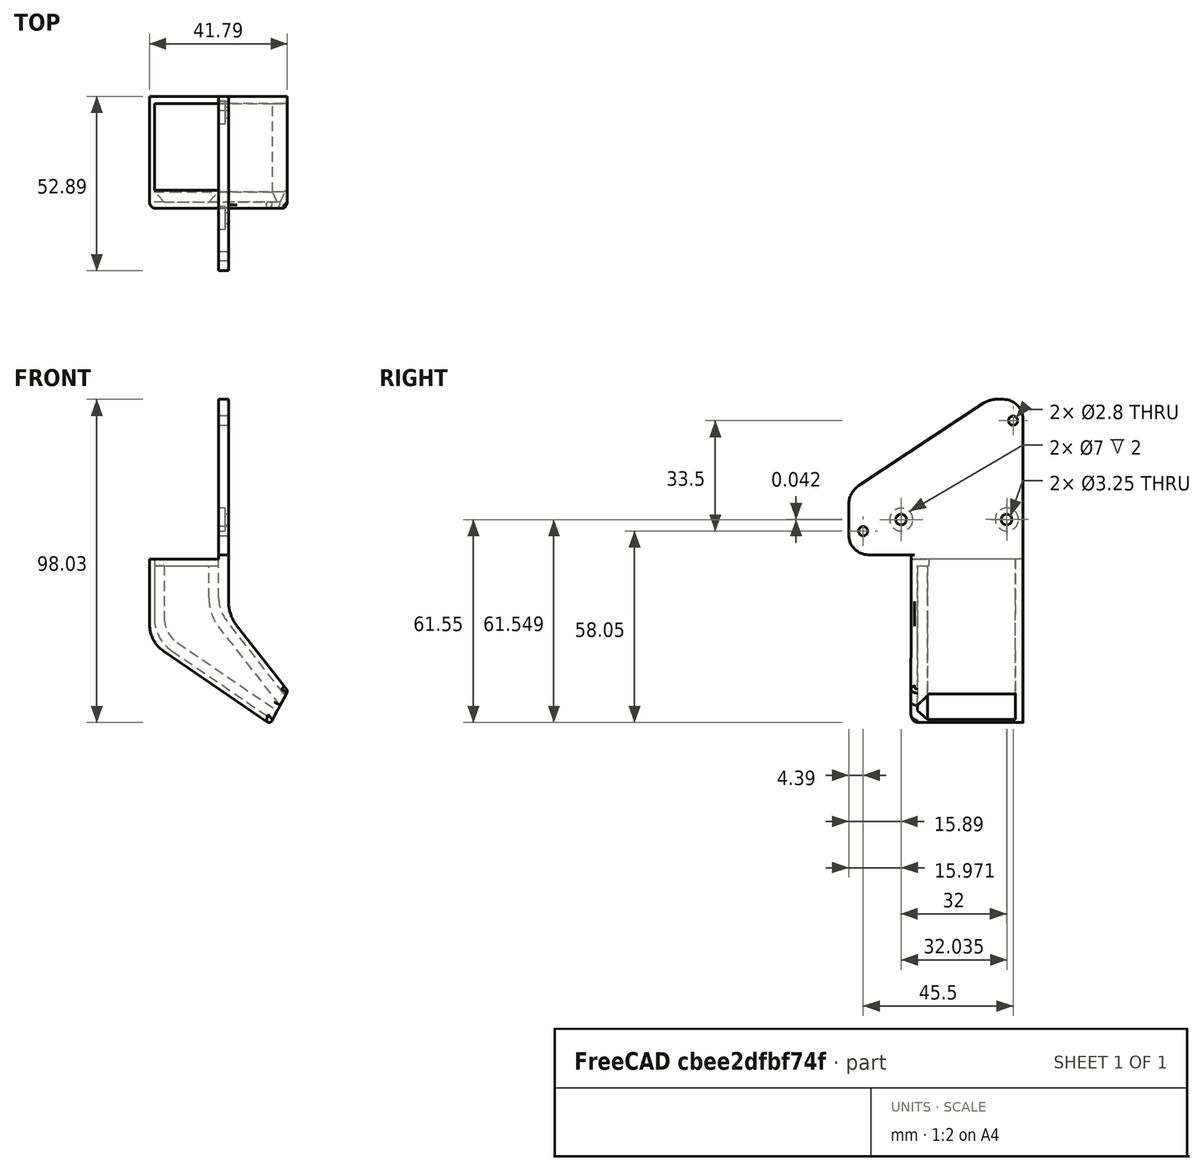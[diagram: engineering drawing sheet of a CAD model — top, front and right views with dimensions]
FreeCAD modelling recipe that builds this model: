
FCSTD DOCUMENT  (FreeCAD 0.19R)
Label: FanDuct10.1
License: All rights reserved
LicenseURL: http://en.wikipedia.org/wiki/All_rights_reserved
objects: Sketcher::SketchObject×10, PartDesign::Fillet×10, PartDesign::Pocket×5, PartDesign::Pad×3, PartDesign::Chamfer×2, PartDesign::Body×1, Mesh::Feature×1
note: 51 computed .brp shape members not serialized (recipe doc carries the construction recipe); baked Part::Feature solids carry a one-line shape summary decoded from their .brp

FEATURE [Sketcher::SketchObject] Sketch035  label="startingpos"
  FullyConstrained = false
  MapMode = 5
  Placement = pos=(-14,0,0) rot=(0.57735,-0.57735,-0.57735;2.0944rad)
  sketch-geometry (5):
    g0: Circle CenterX=35 CenterY=-20 CenterZ=0 NormalX=0 NormalY=0 NormalZ=1 AngleXU=0 Radius=1
    g1: Circle CenterX=12 CenterY=44 CenterZ=0 NormalX=0 NormalY=0 NormalZ=1 AngleXU=0 Radius=1.9
    g2: Circle CenterX=55 CenterY=44 CenterZ=0 NormalX=0 NormalY=0 NormalZ=1 AngleXU=0 Radius=1.9
    g3: LineSegment StartX=12.5 StartY=38 StartZ=0 EndX=35 EndY=38 EndZ=0
    g4: GeomPoint X=35 Y=-19 Z=0
  constraints (13):
    c: DistanceY(g0) = -20
    c: Diameter(g1) = 3.8
    c: Equal(g1,g2)
    c: DistanceY(g1) = 44
    c: DistanceX(g2) = 55
    c: DistanceY(g2) = 44
    c: Diameter(g0) = 2
    c: Horizontal(g3)
    c: Distance(g3) = 22.5
    c: DistanceX(g0) = 35
    c: DistanceX(g3) = 35
    c: DistanceY(g3) = 38
    c: DistanceX(g4) = 35
FEATURE [Sketcher::SketchObject] Sketch037  label="startingpos001"
  FullyConstrained = false
  MapMode = 5
  Placement = pos=(-35,0,2e-15) rot=(0.57735,-0.57735,-0.57735;2.0944rad)
  sketch-geometry (11):
    g0: Circle CenterX=35 CenterY=-20 CenterZ=0 NormalX=0 NormalY=0 NormalZ=1 AngleXU=0 Radius=1
    g1: Circle CenterX=12 CenterY=44 CenterZ=0 NormalX=0 NormalY=0 NormalZ=1 AngleXU=0 Radius=1.9
    g2: Circle CenterX=55 CenterY=44 CenterZ=0 NormalX=0 NormalY=0 NormalZ=1 AngleXU=0 Radius=1.9
    g3: LineSegment StartX=12.5 StartY=38 StartZ=0 EndX=35 EndY=38 EndZ=0
    g4: LineSegment StartX=5.72016 StartY=54.4932 StartZ=0 EndX=25.1498 EndY=-38.5121 EndZ=0
    g5: LineSegment StartX=25.1498 StartY=-38.5121 StartZ=0 EndX=-60.2156 EndY=-38.5121 EndZ=0
    g6: LineSegment StartX=-60.2156 StartY=-38.5121 StartZ=0 EndX=-35.1899 EndY=60.5708 EndZ=0
    g7: LineSegment StartX=-35.1899 StartY=60.5708 StartZ=0 EndX=99.6909 EndY=60.5708 EndZ=0
    g8: LineSegment StartX=56.1815 StartY=-38.9405 StartZ=0 EndX=37.0599 EndY=52.5904 EndZ=0
    g9: LineSegment StartX=56.1815 StartY=-38.9405 StartZ=0 EndX=99.6909 EndY=60.5708 EndZ=0
    g10: LineSegment StartX=5.72016 StartY=54.4932 StartZ=0 EndX=37.0599 EndY=52.5904 EndZ=0
  constraints (27):
    c: DistanceY(g0) = -20
    c: Diameter(g1) = 3.8
    c: Equal(g1,g2)
    c: DistanceX(g1) = 12
    c: DistanceY(g1) = 44
    c: DistanceX(g2) = 55
    c: DistanceY(g2) = 44
    c: Diameter(g0) = 2
    c: Horizontal(g3)
    c: Distance(g3) = 22.5
    c: DistanceX(g0) = 35
    c: DistanceX(g3) = 35
    c: DistanceY(g3) = 38
    c: Horizontal(g5)
    c: Coincident(g5,g6)
    c: Coincident(g6,g7)
    c: Horizontal(g7)
    c: Distance(g3,g8) = 5
    c: Coincident(g5,g4)
    c: Coincident(g8,g9)
    c: Coincident(g9,g7)
    c: DistanceX(g7) = 99.6909
    c: DistanceY(g7) = 60.5708
    c: DistanceX(g6) = -35.1899
    c: Parallel(g8,g4)
    c: Coincident(g10,g4)
    c: Coincident(g10,g8)
FEATURE [Sketcher::SketchObject] Sketch  label="Body001"
  FullyConstrained = false
  MapMode = 5
  Placement = pos=(0,0,0) rot=(1,0,0;1.5708rad)
  Support = -> [XZ_Plane]
  sketch-geometry (14):
    g0: LineSegment StartX=0 StartY=35 StartZ=0 EndX=-3 EndY=35 EndZ=0
    g1: LineSegment StartX=-3 StartY=35 StartZ=0 EndX=-3 EndY=-15 EndZ=0
    g2: LineSegment StartX=-3 StartY=-15 StartZ=0 EndX=-24 EndY=-15 EndZ=0
    g3: LineSegment StartX=-24 StartY=-15 StartZ=0 EndX=-24 EndY=-40 EndZ=0
    g4: GeomPoint X=25 Y=-66 Z=0
    g5: LineSegment StartX=0 StartY=0 StartZ=0 EndX=53.43 EndY=0 EndZ=0
    g6: LineSegment StartX=53.43 StartY=0 StartZ=0 EndX=53.43 EndY=-30 EndZ=0
    g7: LineSegment StartX=53.43 StartY=-30 StartZ=0 EndX=0 EndY=-30 EndZ=0
    g8: LineSegment StartX=0 StartY=-30 StartZ=0 EndX=0 EndY=0 EndZ=0
    g9: LineSegment StartX=0 StartY=0 StartZ=0 EndX=0 EndY=-32 EndZ=0
    g10: LineSegment StartX=0 StartY=-32 StartZ=0 EndX=18 EndY=-55 EndZ=0
    g11: LineSegment StartX=-24 StartY=-40 StartZ=0 EndX=12.6411 EndY=-65 EndZ=0
    g12: LineSegment StartX=12.6411 StartY=-65 StartZ=0 EndX=18 EndY=-55 EndZ=0
    g13: LineSegment StartX=0 StartY=35 StartZ=0 EndX=0 EndY=0 EndZ=0
  constraints (38):
    c: PointOnObject(g0,g-2)
    c: Coincident(g0,g1)
    c: Vertical(g1)
    c: Coincident(g1,g2)
    c: Horizontal(g2)
    c: Coincident(g2,g3)
    c: Vertical(g3)
    c: Horizontal(g0)
    c: Distance(g0) = 3
    c: DistanceX(g4) = 25
    c: DistanceY(g4) = -66
    c: Distance(g2) = 21
    c: Distance(g3) = 25
    c: DistanceY(g1) = -15
    c: Distance(g1) = 50
    c: Coincident(g5,g6)
    c: Coincident(g6,g7)
    c: Coincident(g7,g8)
    c: Coincident(g8,g5)
    c: Horizontal(g5)
    c: Horizontal(g7)
    c: Vertical(g6)
    c: Vertical(g8)
    c: DistanceY(g6) = -30
    c: Coincident(g5,g-1)
    c: Coincident(g-1,g9)
    c: Vertical(g9)
    c: Coincident(g9,g10)
    c: DistanceY(g4,g10) = 11
    c: DistanceX(g10,g4) = 7
    c: Coincident(g11,g3)
    c: DistanceY(g11,g4) = -1
    c: Coincident(g11,g12)
    c: Coincident(g12,g10)
    c: Distance(g9,g7) = 2
    c: DistanceX(g6) = 53.43
    c: Coincident(g0,g13)
    c: Coincident(g13,g9)
FEATURE [PartDesign::Pad] Pad
  Direction = (1,1,1)
  Length = 70
  Length2 = 100
  Placement = pos=(0,0,0) rot=(1,0,0;1.5708rad)
  Profile = -> Sketch
  Type = 0
FEATURE [Sketcher::SketchObject] Sketch052  label="Mountholes"
  FullyConstrained = true
  MapMode = 5
  Placement = pos=(-3,0,0) rot=(0.707107,0,-0.707107;3.14159rad)
  Support = -> [Pad]
  sketch-geometry (2):
    g0: Circle CenterX=3 CenterY=20 CenterZ=0 NormalX=0 NormalY=0 NormalZ=1 AngleXU=0 Radius=1.625
    g1: Circle CenterX=3 CenterY=52 CenterZ=0 NormalX=0 NormalY=0 NormalZ=1 AngleXU=0 Radius=1.625
  constraints (6):
    c: Diameter(g1) = 3.25
    c: Equal(g1,g0)
    c: DistanceY(g0) = 20
    c: DistanceX(g0) = 3
    c: DistanceX(g1) = 3
    c: Distance(g0,g1) = 32
FEATURE [PartDesign::Pocket] Pocket
  BaseFeature = -> Pad
  Length = 5
  Length2 = 100
  Placement = pos=(0,0,0) rot=(1,0,0;1.5708rad)
  Profile = -> Sketch052
  Type = 0
FEATURE [Sketcher::SketchObject] Sketch062  label="outlineCut"
  ExternalGeometry = -> [Pocket]
  FullyConstrained = false
  MapMode = 5
  Placement = pos=(-3,0,0) rot=(0.707107,0,-0.707107;3.14159rad)
  Support = -> [Pocket]
  sketch-geometry (17):
    g0: LineSegment StartX=67 StartY=15 StartZ=0 EndX=14.3821 EndY=15 EndZ=0
    g1: LineSegment StartX=14.3821 StartY=15 StartZ=0 EndX=-3.25457 EndY=15 EndZ=0
    g2: LineSegment StartX=-3.25457 StartY=15 StartZ=0 EndX=-33.4784 EndY=15 EndZ=0
    g3: LineSegment StartX=-33.4784 StartY=15 StartZ=0 EndX=-33.4784 EndY=25.1764 EndZ=0
    g4: LineSegment StartX=-33.4784 StartY=25.1764 StartZ=0 EndX=-5.24318 EndY=67.8892 EndZ=0
    g5: LineSegment StartX=-5.24318 StartY=67.8892 StartZ=0 EndX=13.6612 EndY=67.8892 EndZ=0
    g6: LineSegment StartX=13.6612 StartY=67.8892 StartZ=0 EndX=13.6612 EndY=48.9924 EndZ=0
    g7: LineSegment StartX=13.6612 StartY=48.9924 StartZ=0 EndX=67 EndY=49 EndZ=0
    g8: LineSegment StartX=67 StartY=49 StartZ=0 EndX=67 EndY=15 EndZ=0
    g9: Circle CenterX=67 CenterY=30 CenterZ=0 NormalX=0 NormalY=0 NormalZ=1 AngleXU=0 Radius=2.43328
    g10: Circle CenterX=14.0216 CenterY=31.9962 CenterZ=0 NormalX=0 NormalY=0 NormalZ=1 AngleXU=0 Radius=1.32268
    g11: LineSegment StartX=67 StartY=49 StartZ=0 EndX=69.9693 EndY=84.1734 EndZ=0
    g12: LineSegment StartX=69.9693 StartY=84.1734 StartZ=0 EndX=11.0977 EndY=87.4268 EndZ=0
    g13: LineSegment StartX=11.0977 StartY=87.4268 StartZ=0 EndX=-68.9986 EndY=87.4268 EndZ=0
    g14: LineSegment StartX=-68.9986 StartY=87.4268 StartZ=0 EndX=-68.9986 EndY=-45.6539 EndZ=0
    g15: LineSegment StartX=-68.9986 StartY=-45.6539 StartZ=0 EndX=88.0955 EndY=-45.6539 EndZ=0
    g16: LineSegment StartX=88.0955 StartY=-45.6539 StartZ=0 EndX=67 EndY=15 EndZ=0
  constraints (32):
    c: Horizontal(g1)
    c: Coincident(g1,g2)
    c: Coincident(g2,g3)
    c: Vertical(g3)
    c: Coincident(g3,g4)
    c: Coincident(g4,g5)
    c: Horizontal(g5)
    c: Coincident(g5,g6)
    c: Vertical(g6)
    c: Coincident(g6,g7)
    c: Coincident(g7,g8)
    c: Coincident(g8,g0)
    c: Vertical(g8)
    c: DistanceY(g-3,g9) = 10
    c: DistanceX(g-3,g9) = 64
    c: Distance(g8) = 34
    c: Symmetric(g0,g6,g10)
    c: Distance(g0,g6) = 34
    c: DistanceY(g0,g-3) = 5
    c: Horizontal(g0)
    c: Coincident(g7,g11)
    c: Coincident(g11,g12)
    c: Coincident(g12,g13)
    c: Horizontal(g13)
    c: Coincident(g13,g14)
    c: Vertical(g14)
    c: Coincident(g14,g15)
    c: Horizontal(g15)
    c: Coincident(g15,g16)
    c: Coincident(g16,g0)
    c: Coincident(g1,g0)
    c: Horizontal(g2)
FEATURE [PartDesign::Pocket] Pocket001
  BaseFeature = -> Pocket
  Length = 29
  Length2 = 100
  Placement = pos=(0,0,0) rot=(1,0,0;1.5708rad)
  Profile = -> Sketch062
  Type = 4
FEATURE [Sketcher::SketchObject] Sketch061  label="cavity"
  ExternalGeometry = -> [Pocket]
  FullyConstrained = true
  MapMode = 5
  Placement = pos=(0,-15,-3.3e-15) rot=(-1,0,0;1.5708rad)
  Support = -> [Pocket001]
  sketch-geometry (6):
    g0: LineSegment StartX=-3 StartY=15 StartZ=0 EndX=-22.5 EndY=15 EndZ=0
    g1: LineSegment StartX=-22.5 StartY=15 StartZ=0 EndX=-22.5 EndY=39.2076 EndZ=0
    g2: LineSegment StartX=-3 StartY=30.6005 StartZ=0 EndX=-3 EndY=15 EndZ=0
    g3: LineSegment StartX=-22.5 StartY=39.2076 StartZ=0 EndX=13.9616 EndY=64.0851 EndZ=0
    g4: LineSegment StartX=13.9616 StartY=64.0851 StartZ=0 EndX=18.267 EndY=57.775 EndZ=0
    g5: LineSegment StartX=18.267 StartY=57.775 StartZ=0 EndX=-3 EndY=30.6005 EndZ=0
  constraints (17):
    c: Horizontal(g0)
    c: Coincident(g0,g1)
    c: Vertical(g1)
    c: Coincident(g2,g0)
    c: Vertical(g2)
    c: Coincident(g1,g3)
    c: Coincident(g3,g4)
    c: Coincident(g4,g5)
    c: Coincident(g5,g2)
    c: Distance(g2,g-3) = 1.5
    c: Distance(g-4,g3) = 1.5
    c: Distance(g-3,g5) = 1.5
    c: Distance(g1,g-4) = 1.5
    c: Distance(g1,g-5) = 1.5
    c: Coincident(g0,g-6)
    c: Perpendicular(g4,g3)
    c: Distance(g3) = 44.14
FEATURE [PartDesign::Pocket] Pocket002
  BaseFeature = -> Pocket001
  Length = 32
  Length2 = 100
  Placement = pos=(0,0,0) rot=(1,0,0;1.5708rad)
  Profile = -> Sketch061
  Type = 0
FEATURE [Sketcher::SketchObject] Sketch064  label="cap"
  ExternalGeometry = -> [Pocket002]
  FullyConstrained = false
  MapMode = 5
  Placement = pos=(0,-15,-3.3e-15) rot=(-1,0,0;1.5708rad)
  Support = -> [Pocket002]
  sketch-geometry (6):
    g0: LineSegment StartX=17.2258 StartY=56.4446 StartZ=0 EndX=-2.74511 EndY=30.8096 EndZ=0
    g1: LineSegment StartX=-2.74511 StartY=30.8096 StartZ=0 EndX=-2.74511 EndY=15 EndZ=0
    g2: LineSegment StartX=-2.74511 StartY=15 StartZ=0 EndX=-22.6238 EndY=15 EndZ=0
    g3: LineSegment StartX=-22.6238 StartY=15 StartZ=0 EndX=-22.6238 EndY=39.3012 EndZ=0
    g4: LineSegment StartX=-22.6238 StartY=39.3012 StartZ=0 EndX=13.3537 EndY=63.6703 EndZ=0
    g5: LineSegment StartX=13.3537 StartY=63.6703 StartZ=0 EndX=17.2258 EndY=56.4446 EndZ=0
  constraints (11):
    c: Coincident(g0,g1)
    c: Vertical(g1)
    c: Coincident(g1,g2)
    c: Horizontal(g2)
    c: Coincident(g2,g3)
    c: Vertical(g3)
    c: Coincident(g3,g4)
    c: Coincident(g4,g5)
    c: Coincident(g5,g0)
    c: Coincident(g0,g-4)
    c: Coincident(g-3,g4)
FEATURE [PartDesign::Pad] Pad001
  BaseFeature = -> Pocket002
  Direction = (1,1,1)
  Length = 2.25
  Length2 = 100
  Placement = pos=(0,0,0) rot=(1,0,0;1.5708rad)
  Profile = -> Sketch064
  Reversed = true
  Type = 0
FEATURE [Sketcher::SketchObject] Sketch066  label="fanholes"
  FullyConstrained = true
  MapMode = 5
  Placement = pos=(-3,0,0) rot=(0.707107,0,-0.707107;3.14159rad)
  Support = -> [Pad001]
  sketch-geometry (2):
    g0: Circle CenterX=-27 CenterY=18 CenterZ=0 NormalX=0 NormalY=0 NormalZ=1 AngleXU=0 Radius=1.4
    g1: Circle CenterX=6.5 CenterY=63.5 CenterZ=0 NormalX=0 NormalY=0 NormalZ=1 AngleXU=0 Radius=1.4
  constraints (6):
    c: Diameter(g0) = 2.8
    c: Equal(g0,g1)
    c: DistanceX(g1) = 6.5
    c: DistanceY(g1) = 63.5
    c: DistanceX(g0) = -27
    c: DistanceY(g0) = 18
FEATURE [PartDesign::Pocket] Pocket003
  BaseFeature = -> Pad001
  Length = 5
  Length2 = 100
  Placement = pos=(0,0,0) rot=(1,0,0;1.5708rad)
  Profile = -> Sketch066
  Type = 0
FEATURE [Sketcher::SketchObject] Sketch068  label="Countersink"
  FullyConstrained = false
  MapMode = 5
  Placement = pos=(-3,0,0) rot=(0.707107,0,-0.707107;3.14159rad)
  sketch-geometry (2):
    g0: Circle CenterX=2.95829 CenterY=19.8839 CenterZ=0 NormalX=0 NormalY=0 NormalZ=1 AngleXU=0 Radius=3.5
    g1: Circle CenterX=3.00051 CenterY=51.9186 CenterZ=0 NormalX=0 NormalY=0 NormalZ=1 AngleXU=0 Radius=3.5
  constraints (2):
    c: Diameter(g0) = 7
    c: Equal(g0,g1)
FEATURE [PartDesign::Pocket] Pocket004
  BaseFeature = -> Pocket003
  Length = 2
  Length2 = 100
  Placement = pos=(0,0,0) rot=(1,0,0;1.5708rad)
  Profile = -> Sketch068
  Type = 0
FEATURE [Sketcher::SketchObject] Sketch069
  ExternalGeometry = -> [Pocket004]
  FullyConstrained = false
  MapMode = 5
  Placement = pos=(0,3.3e-15,-15) rot=(0,0,1;3.14159rad)
  Support = -> [Pocket004]
  sketch-geometry (4):
    g0: LineSegment StartX=2.67092 StartY=47.2907 StartZ=0 EndX=23.0703 EndY=47.2907 EndZ=0
    g1: LineSegment StartX=23.0703 StartY=47.2907 StartZ=0 EndX=23.0703 EndY=43.45 EndZ=0
    g2: LineSegment StartX=23.0703 StartY=43.45 StartZ=0 EndX=2.67092 EndY=43.45 EndZ=0
    g3: LineSegment StartX=2.67092 StartY=43.45 StartZ=0 EndX=2.67092 EndY=47.2907 EndZ=0
  constraints (9):
    c: Coincident(g0,g1)
    c: Coincident(g1,g2)
    c: Coincident(g2,g3)
    c: Coincident(g3,g0)
    c: Horizontal(g0)
    c: Horizontal(g2)
    c: Vertical(g1)
    c: Vertical(g3)
    c: Distance(g-3,g2) = 26.2
FEATURE [PartDesign::Pad] Pad002
  BaseFeature = -> Pocket004
  Direction = (1,1,1)
  Length = 2
  Length2 = 100
  Placement = pos=(0,0,0) rot=(1,0,0;1.5708rad)
  Profile = -> Sketch069
  Reversed = true
  Type = 0
FEATURE [PartDesign::Fillet] Fillet
  Base = -> Pad002 [Edge97]
  BaseFeature = -> Pad002
  Placement = pos=(0,0,0) rot=(1,0,0;1.5708rad)
  Radius = 12
  SupportTransform = false
FEATURE [PartDesign::Fillet] Fillet001
  Base = -> Fillet [Edge50]
  BaseFeature = -> Fillet
  Placement = pos=(0,0,0) rot=(1,0,0;1.5708rad)
  Radius = 12
  SupportTransform = false
FEATURE [PartDesign::Fillet] Fillet002
  Base = -> Fillet001 [Edge107]
  BaseFeature = -> Fillet001
  Placement = pos=(0,0,0) rot=(1,0,0;1.5708rad)
  Radius = 10
  SupportTransform = false
FEATURE [PartDesign::Fillet] Fillet003
  Base = -> Fillet002 [Edge75]
  BaseFeature = -> Fillet002
  Placement = pos=(0,0,0) rot=(1,0,0;1.5708rad)
  Radius = 11
  SupportTransform = false
FEATURE [PartDesign::Fillet] Fillet004
  Base = -> Fillet003 [Edge21]
  BaseFeature = -> Fillet003
  Placement = pos=(0,0,0) rot=(1,0,0;1.5708rad)
  Radius = 1
  SupportTransform = false
FEATURE [PartDesign::Chamfer] Chamfer
  Angle = 45
  Base = -> Fillet004 [Edge36]
  BaseFeature = -> Fillet004
  ChamferType = 0
  FlipDirection = false
  Placement = pos=(0,0,0) rot=(1,0,0;1.5708rad)
  Size = 3
  Size2 = 1
  SupportTransform = false
FEATURE [PartDesign::Chamfer] Chamfer001
  Angle = 45
  Base = -> Chamfer [Edge13]
  BaseFeature = -> Chamfer
  ChamferType = 0
  FlipDirection = false
  Placement = pos=(0,0,0) rot=(1,0,0;1.5708rad)
  Size = 3
  Size2 = 1
  SupportTransform = false
FEATURE [PartDesign::Fillet] Fillet005
  Base = -> Chamfer001 [Edge5]
  BaseFeature = -> Chamfer001
  Placement = pos=(0,0,0) rot=(1,0,0;1.5708rad)
  Radius = 0.6
  SupportTransform = false
FEATURE [PartDesign::Fillet] Fillet006
  Base = -> Fillet005 [Edge40]
  BaseFeature = -> Fillet005
  Placement = pos=(0,0,0) rot=(1,0,0;1.5708rad)
  Radius = 2
  SupportTransform = false
FEATURE [PartDesign::Fillet] Fillet007
  Base = -> Fillet006 [Edge11]
  BaseFeature = -> Fillet006
  Placement = pos=(0,0,0) rot=(1,0,0;1.5708rad)
  Radius = 1.1
  SupportTransform = false
FEATURE [PartDesign::Fillet] Fillet008
  Base = -> Fillet007 [Edge157,Edge129]
  BaseFeature = -> Fillet007
  Placement = pos=(0,0,0) rot=(1,0,0;1.5708rad)
  Radius = 6
  SupportTransform = false
FEATURE [PartDesign::Fillet] Fillet009
  Base = -> Fillet008 [Edge20,Edge73]
  BaseFeature = -> Fillet008
  Placement = pos=(0,0,0) rot=(1,0,0;1.5708rad)
  Radius = 7
  SupportTransform = false
FEATURE [PartDesign::Body] Body
  Group = -> [Sketch035,Sketch037,Sketch,Pad,Sketch052,Sketch061,Pocket,Sketch062,Pocket001,Sketch064,Sketch066,Pocket002,Pad001,Pocket003,Sketch068,Pocket004,Sketch069,Pad002,Fillet,Fillet001,Fillet002,Fillet003,Fillet004,Chamfer,Chamfer001,Fillet005,Fillet006,Fillet007,Fillet008,Fillet009]
  Origin = -> Origin
  Tip = -> Fillet009
FEATURE [Mesh::Feature] Mesh  label="Fillet009 (Meshed)"
